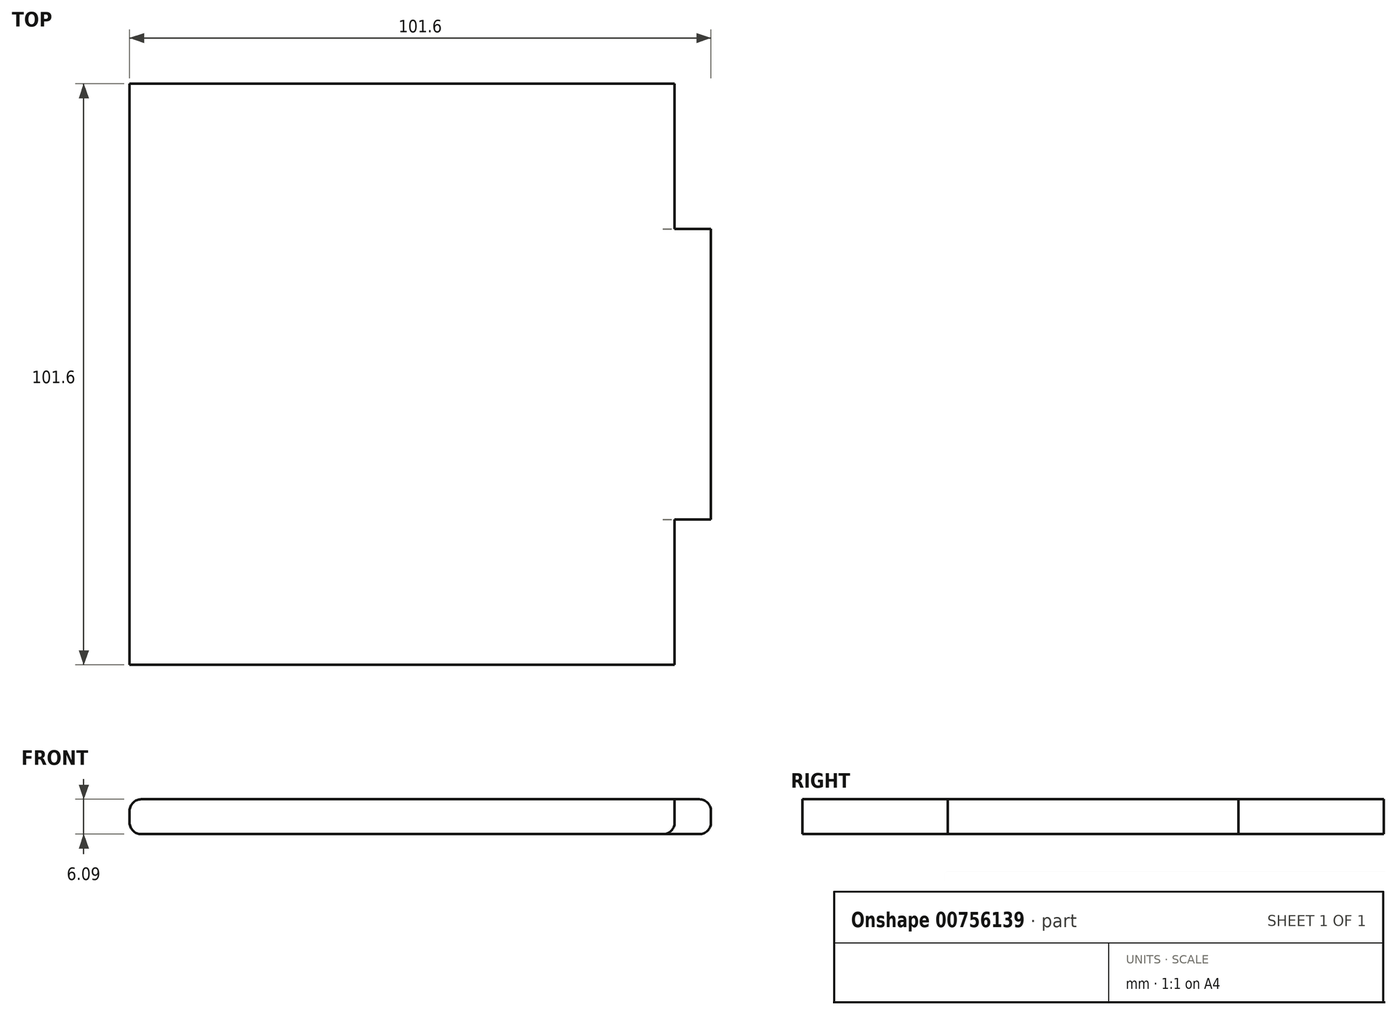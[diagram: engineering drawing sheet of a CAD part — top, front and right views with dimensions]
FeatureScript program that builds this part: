
annotation { "Feature Type Name" : "Feature", "Feature Type Description" : "" }
export const myFeature = defineFeature(function(context is Context, id is Id, definition is map)
    precondition{}
    {
        {
            var Q0;
            Q0=qCreatedBy(makeId("Front.planeOp"),FACE);
            var sketch = newSketch(context, id + "F0", { "sketchPlane" : qUnion([Q0])});
            skLineSegment(sketch, "E0.bottom", {"start": v(-48.33, 19.22) * mm, "end": v(53.27, 19.22) * mm});
            skLineSegment(sketch, "E0.top", {"start": v(-48.33, 13.13) * mm, "end": v(53.27, 13.13) * mm});
            skLineSegment(sketch, "E0.left", {"start": v(-48.33, 19.22) * mm, "end": v(-48.33, 13.13) * mm});
            skLineSegment(sketch, "E0.right", {"start": v(53.27, 19.22) * mm, "end": v(53.27, 13.13) * mm});
            skSolve(sketch);
        }
        {
            var Q0;
            Q0 = qSketchRegion(id + "F0", true);
            extrude(context, id + "F1", {"entities" : qUnion([Q0]), "depth" : 101.6 * mm, "offsetDistance" : 25.4 * mm});
        }
        {
            var Q0;
            Q0=makeQuery(id+"F1.opExtrude","SWEPT_FACE",FACE,{"disambiguationData":[OSD([sQuery(id+"F0.wireOp",EDGE,"E0.bottom")])]});
            var sketch = newSketch(context, id + "F2", { "sketchPlane" : qUnion([Q0])});
            skLineSegment(sketch, "E1.bottom", {"start": v(-48.33, 0) * mm, "end": v(53.27, 0) * mm});
            skLineSegment(sketch, "E1.top", {"start": v(-48.33, -101.6) * mm, "end": v(53.27, -101.6) * mm});
            skLineSegment(sketch, "E1.left", {"start": v(-48.33, 0) * mm, "end": v(-48.33, -101.6) * mm});
            skLineSegment(sketch, "E1.right", {"start": v(53.27, 0) * mm, "end": v(53.27, -101.6) * mm});
            skLineSegment(sketch, "E2.bottom", {"start": v(-48.33, -25.4) * mm, "end": v(53.27, -25.4) * mm});
            skLineSegment(sketch, "E2.top", {"start": v(-48.33, -76.2) * mm, "end": v(53.27, -76.2) * mm});
            skLineSegment(sketch, "E2.left", {"start": v(-48.33, -25.4) * mm, "end": v(-48.33, -76.2) * mm});
            skLineSegment(sketch, "E2.right", {"start": v(53.27, -25.4) * mm, "end": v(53.27, -76.2) * mm});
            skPoint(sketch, "E2.middle", {"position": v(2.47, -50.8) * mm});
            skPoint(sketch, "E2.middle.positionSnap0", {"position": v(-48.33, -50.8) * mm});
            skPoint(sketch, "E2.middle.positionSnap1", {"position": v(2.47, 0) * mm});
            skPoint(sketch, "E2.centerSnap0", {"position": v(-48.33, -50.8) * mm});
            skPoint(sketch, "E2.centerSnap1", {"position": v(2.47, 0) * mm});
            skLineSegment(sketch, "E3.bottom", {"start": v(-41.98, -25.4) * mm, "end": v(46.92, -25.4) * mm});
            skLineSegment(sketch, "E3.top", {"start": v(-41.98, -76.2) * mm, "end": v(46.92, -76.2) * mm});
            skLineSegment(sketch, "E3.left", {"start": v(-41.98, -25.4) * mm, "end": v(-41.98, -76.2) * mm});
            skLineSegment(sketch, "E3.right", {"start": v(46.92, -25.4) * mm, "end": v(46.92, -76.2) * mm});
            skLineSegment(sketch, "E4", {"start": v(46.92, -25.4) * mm, "end": v(46.92, 0) * mm});
            skLineSegment(sketch, "E5", {"start": v(46.92, -76.2) * mm, "end": v(46.92, -101.6) * mm});
            skSolve(sketch);
        }
        {
            var Q0;
            {var subQ0=sQuery(id+"F2.wireOp",EDGE,"E2.left");Q0=makeQuery(id+"F2.imprint","IMPRINT",FACE,{"disambiguationData":[TD([[makeQuery(id+"F2.imprint","IMPRINT",EDGE,{"derivedFrom":subQ0}),-1.0]])]});}
            var Q1;
            {var subQ3=sQuery(id+"F2.wireOp",EDGE,"E4");Q1=makeQuery(id+"F2.imprint","IMPRINT",FACE,{"disambiguationData":[TD([[makeQuery(id+"F2.imprint","IMPRINT",EDGE,{"derivedFrom":subQ3}),-1.0]])]});}
            var Q2;
            {var subQ3=sQuery(id+"F2.wireOp",EDGE,"E5");Q2=makeQuery(id+"F2.imprint","IMPRINT",FACE,{"disambiguationData":[TD([[makeQuery(id+"F2.imprint","IMPRINT",EDGE,{"derivedFrom":subQ3}),1.0]])]});}
            extrude(context, id + "F3", {"entities" : qUnion([Q0, Q1, Q2]), "operationType" : NewBodyOperationType.REMOVE, "oppositeDirection" : true, "depth" : 25.4 * mm, "offsetDistance" : 25.4 * mm});
        }
        {
            var Q0;
            Q0=makeQuery(id+"F1.opExtrude","SWEPT_EDGE",EDGE,{"disambiguationData":[OSD([sQuery(id+"F0.wireOp",EDGE,"E0.bottom"),sQuery(id+"F0.wireOp",EDGE,"E0.right")])]});
            var Q1;
            Q1=makeQuery(id+"F3.boolean.opBoolean","COPY",EDGE,{"derivedFrom":makeQuery(id+"F3.opExtrude","CAP_EDGE",EDGE,{"disambiguationData":[OSD([sQuery(id+"F2.wireOp",EDGE,"E5")])],"isStart":true})});
            var Q2;
            Q2=makeQuery(id+"F3.boolean.opBoolean","COPY",EDGE,{"derivedFrom":makeQuery(id+"F3.opExtrude","CAP_EDGE",EDGE,{"disambiguationData":[OSD([sQuery(id+"F2.wireOp",EDGE,"E4")])],"isStart":true})});
            var Q3;
            Q3=makeQuery(id+"F1.opExtrude","SWEPT_EDGE",EDGE,{"disambiguationData":[OSD([sQuery(id+"F0.wireOp",EDGE,"E0.top"),sQuery(id+"F0.wireOp",EDGE,"E0.right")])]});
            var Q4;
            Q4=makeQuery(id+"F3.boolean.opBoolean","INTERSECT",EDGE,{"derivedFrom":[makeQuery(id+"F1.opExtrude","SWEPT_FACE",FACE,{"disambiguationData":[OSD([sQuery(id+"F0.wireOp",EDGE,"E0.top")])]}),makeQuery(id+"F3.opExtrude","SWEPT_FACE",FACE,{"disambiguationData":[OSD([sQuery(id+"F2.wireOp",EDGE,"E4")])]})]});
            var Q5;
            Q5=makeQuery(id+"F3.boolean.opBoolean","INTERSECT",EDGE,{"derivedFrom":[makeQuery(id+"F1.opExtrude","SWEPT_FACE",FACE,{"disambiguationData":[OSD([sQuery(id+"F0.wireOp",EDGE,"E0.top")])]}),makeQuery(id+"F3.opExtrude","SWEPT_FACE",FACE,{"disambiguationData":[OSD([sQuery(id+"F2.wireOp",EDGE,"E5")])]})]});
            var Q6;
            Q6=makeQuery(id+"F3.boolean.opBoolean","COPY",EDGE,{"derivedFrom":makeQuery(id+"F3.opExtrude","CAP_EDGE",EDGE,{"disambiguationData":[OSD([sQuery(id+"F2.wireOp",EDGE,"E3.left")])],"isStart":true})});
            var Q7;
            {var subQ0=sQuery(id+"F0.wireOp",EDGE,"E0.bottom");var subQ1=sQuery(id+"F0.wireOp",EDGE,"E0.left");var subQ2=sQuery(id+"F2.wireOp",EDGE,"E2.bottom");Q7=makeQuery(id+"F3.boolean.opBoolean","SPLIT",EDGE,{"disambiguationData":[TD([makeQuery(id+"F3.opExtrude","SWEPT_FACE",FACE,{"disambiguationData":[OSD([subQ2]),TDD([makeQuery(id+"F2.imprint","IMPRINT",EDGE,{"disambiguationData":[TD([[makeQuery(id+"F2.imprint","INTERSECT",VERTEX,{"derivedFrom":[sQuery(id+"F2.wireOp",EDGE,"E1.left"),subQ2,sQuery(id+"F2.wireOp",EDGE,"E2.left")]}),-1.0]])],"derivedFrom":subQ2})])]})])],"derivedFrom":makeQuery(id+"F1.opExtrude","SWEPT_EDGE",EDGE,{"disambiguationData":[OSD([subQ0,subQ1])]})});}
            var Q8;
            {var subQ0=sQuery(id+"F0.wireOp",EDGE,"E0.bottom");var subQ1=sQuery(id+"F2.wireOp",EDGE,"E2.top");var subQ2=sQuery(id+"F0.wireOp",EDGE,"E0.left");Q8=makeQuery(id+"F3.boolean.opBoolean","SPLIT",EDGE,{"disambiguationData":[TD([makeQuery(id+"F3.opExtrude","SWEPT_FACE",FACE,{"disambiguationData":[OSD([subQ1]),TDD([makeQuery(id+"F2.imprint","IMPRINT",EDGE,{"disambiguationData":[TD([[makeQuery(id+"F2.imprint","INTERSECT",VERTEX,{"derivedFrom":[sQuery(id+"F2.wireOp",EDGE,"E1.left"),subQ1,sQuery(id+"F2.wireOp",EDGE,"E2.left")]}),-1.0]])],"derivedFrom":subQ1})])]})])],"derivedFrom":makeQuery(id+"F1.opExtrude","SWEPT_EDGE",EDGE,{"disambiguationData":[OSD([subQ0,subQ2])]})});}
            var Q9;
            Q9=makeQuery(id+"F3.boolean.opBoolean","INTERSECT",EDGE,{"derivedFrom":[makeQuery(id+"F1.opExtrude","SWEPT_FACE",FACE,{"disambiguationData":[OSD([sQuery(id+"F0.wireOp",EDGE,"E0.top")])]}),makeQuery(id+"F3.opExtrude","SWEPT_FACE",FACE,{"disambiguationData":[OSD([sQuery(id+"F2.wireOp",EDGE,"E3.left")])]})]});
            var Q10;
            {var subQ0=sQuery(id+"F0.wireOp",EDGE,"E0.left");var subQ1=sQuery(id+"F0.wireOp",EDGE,"E0.top");var subQ2=sQuery(id+"F2.wireOp",EDGE,"E2.top");Q10=makeQuery(id+"F3.boolean.opBoolean","SPLIT",EDGE,{"disambiguationData":[TD([makeQuery(id+"F3.opExtrude","SWEPT_FACE",FACE,{"disambiguationData":[OSD([subQ2]),TDD([makeQuery(id+"F2.imprint","IMPRINT",EDGE,{"disambiguationData":[TD([[makeQuery(id+"F2.imprint","INTERSECT",VERTEX,{"derivedFrom":[sQuery(id+"F2.wireOp",EDGE,"E1.left"),subQ2,sQuery(id+"F2.wireOp",EDGE,"E2.left")]}),-1.0]])],"derivedFrom":subQ2})])]})])],"derivedFrom":makeQuery(id+"F1.opExtrude","SWEPT_EDGE",EDGE,{"disambiguationData":[OSD([subQ1,subQ0])]})});}
            var Q11;
            {var subQ0=sQuery(id+"F0.wireOp",EDGE,"E0.left");var subQ1=sQuery(id+"F0.wireOp",EDGE,"E0.top");var subQ2=sQuery(id+"F2.wireOp",EDGE,"E2.bottom");Q11=makeQuery(id+"F3.boolean.opBoolean","SPLIT",EDGE,{"disambiguationData":[TD([makeQuery(id+"F3.opExtrude","SWEPT_FACE",FACE,{"disambiguationData":[OSD([subQ2]),TDD([makeQuery(id+"F2.imprint","IMPRINT",EDGE,{"disambiguationData":[TD([[makeQuery(id+"F2.imprint","INTERSECT",VERTEX,{"derivedFrom":[sQuery(id+"F2.wireOp",EDGE,"E1.left"),subQ2,sQuery(id+"F2.wireOp",EDGE,"E2.left")]}),-1.0]])],"derivedFrom":subQ2})])]})])],"derivedFrom":makeQuery(id+"F1.opExtrude","SWEPT_EDGE",EDGE,{"disambiguationData":[OSD([subQ1,subQ0])]})});}
            fillet(context, id + "F4", {"entities" : qUnion([Q0, Q1, Q2, Q3, Q4, Q5, Q6, Q7, Q8, Q9, Q10, Q11]), "radius" : 2.03 * mm, "tangentPropagation" : true, "allowEdgeOverflow" : false});
        }
    });
